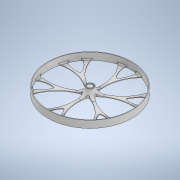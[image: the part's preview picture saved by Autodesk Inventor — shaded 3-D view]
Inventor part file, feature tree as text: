
AUTODESK INVENTOR PART (.ipt)
format: ipt  version: 2020 (Build 240168000, 168)  size: 431,104 bytes
history: native  units: mm
features: pattern_circular x5, fillet x5, extrude x4, sketch x4
ambient origin geometry x8: Origin, YZ Plane, XZ Plane, XY Plane, X Axis, Y Axis, Z Axis, Center Point
bodies: Body1 (feature_tree)
feature tree (18):
  extrude  "Extrusion2"  Depth=96.0mm
  extrude  "Extrusion3"  Depth=28.0mm
  pattern_circular  "Circular Pattern1"  [2 undecoded]
  fillet  "Fillet1"  Radius=7.5mm
  pattern_circular  "Circular Pattern2"  [2 undecoded]
  fillet  "Fillet2"  Radius=12.0mm
  pattern_circular  "Circular Pattern3"  Angle=45.0deg  [1 undecoded]
  fillet  "Fillet3"  Radius=18.0mm
  pattern_circular  "Circular Pattern4"  [2 undecoded]
  extrude  "Extrusion4"  Depth=2.0mm
  extrude  "Extrusion5"  Depth=2.0mm
  fillet  "Fillet4"  Radius=9.0mm
  fillet  "Fillet5"  Radius=9.0mm
  pattern_circular  "Circular Pattern5"  [2 undecoded]
  sketch  "Sketch1"  dims[d6=56.0mm d7=96.0mm]
  sketch  "Sketch2"  dims[d8=48.0mm d9=28.0mm]
  sketch  "Sketch3"  dims[d10=9.0mm]
  sketch  "Sketch4"  dims[d11=1.0mm d12=10.0mm d13=0.0mm d14=7.5mm d15=10.0mm d16=12.0mm d17=45.0deg d22=18.0mm d23=18.0mm d30=60.0mm d31=60.0mm d34=9.0mm d35=9.0mm d36=0.0mm d37=40.0mm d38=1.0mm d39=0.0mm d40=60.0mm d41=360.0deg d43=2.0mm d44=60.0mm d45=360.0deg d47=2.0mm d48=60.0mm d49=360.0deg d51=1.0mm d52=0.0mm d53=2.0mm d54=60.0mm d55=360.0deg d57=12.0mm d58=10.0mm d59=1.0mm d60=0.0mm d61=0.0mm d62=7.5mm d63=10.0mm d64=10.0mm d65=0.0mm d66=10.0mm d67=2.0mm d68=60.0mm d69=360.0deg]
note: 9 required parameter values undecoded (feature->parameter linkage not recoverable at this tier; creation-order binding heuristic only, values carry confidence <= 0.55)
